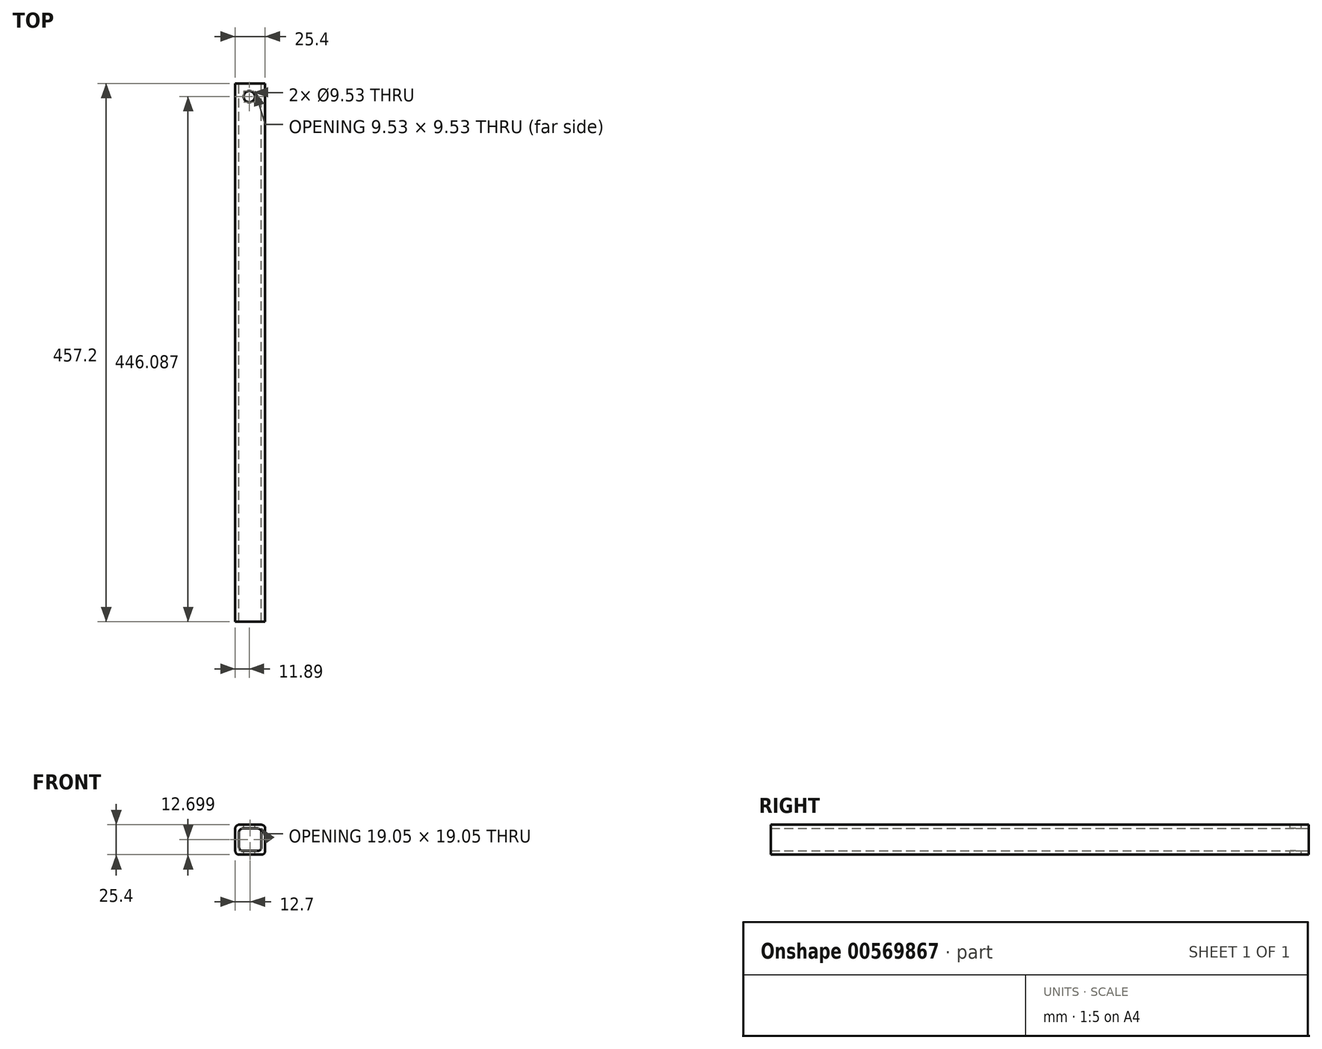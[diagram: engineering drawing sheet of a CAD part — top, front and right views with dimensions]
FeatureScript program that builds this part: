
annotation { "Feature Type Name" : "Feature", "Feature Type Description" : "" }
export const myFeature = defineFeature(function(context is Context, id is Id, definition is map)
    precondition{}
    {
        {
            var Q0;
            Q0=qCreatedBy(makeId("Front.planeOp"),FACE);
            var sketch = newSketch(context, id + "F0", { "sketchPlane" : qUnion([Q0])});
            skLineSegment(sketch, "E0.bottom", {"start": v(10.33, -12.26) * mm, "end": v(-8.72, -12.26) * mm});
            skLineSegment(sketch, "E0.top", {"start": v(10.33, 13.14) * mm, "end": v(-8.72, 13.14) * mm});
            skLineSegment(sketch, "E0.left", {"start": v(13.5, -9.09) * mm, "end": v(13.5, 9.96) * mm});
            skLineSegment(sketch, "E0.right", {"start": v(-11.9, -9.09) * mm, "end": v(-11.9, 9.96) * mm});
            skLineSegment(sketch, "E1.bottom", {"start": v(7.16, -9.09) * mm, "end": v(-5.54, -9.09) * mm});
            skLineSegment(sketch, "E1.top", {"start": v(7.16, 9.96) * mm, "end": v(-5.54, 9.96) * mm});
            skLineSegment(sketch, "E1.left", {"start": v(10.33, -5.91) * mm, "end": v(10.33, 6.79) * mm});
            skLineSegment(sketch, "E1.right", {"start": v(-8.72, -5.91) * mm, "end": v(-8.72, 6.79) * mm});
            skPoint(sketch, "E2.visualSharp", {"position": v(10.33, 9.96) * mm});
            skArc(sketch, "E2.filletArc", {"start": v(10.33, 6.79) * mm, "mid": v(9.4, 9.03) * mm, "end": v(7.16, 9.96) * mm});
            skPoint(sketch, "E3.visualSharp", {"position": v(-8.72, 9.96) * mm});
            skArc(sketch, "E3.filletArc", {"start": v(-5.54, 9.96) * mm, "mid": v(-7.79, 9.03) * mm, "end": v(-8.72, 6.79) * mm});
            skPoint(sketch, "E4.visualSharp", {"position": v(-8.72, -9.09) * mm});
            skArc(sketch, "E4.filletArc", {"start": v(-8.72, -5.91) * mm, "mid": v(-7.79, -8.16) * mm, "end": v(-5.54, -9.09) * mm});
            skPoint(sketch, "E5.visualSharp", {"position": v(10.33, -9.09) * mm});
            skArc(sketch, "E5.filletArc", {"start": v(7.16, -9.09) * mm, "mid": v(9.4, -8.16) * mm, "end": v(10.33, -5.91) * mm});
            skPoint(sketch, "E6.visualSharp", {"position": v(13.5, 13.14) * mm});
            skArc(sketch, "E6.filletArc", {"start": v(13.5, 9.96) * mm, "mid": v(12.58, 12.2) * mm, "end": v(10.33, 13.14) * mm});
            skPoint(sketch, "E7.visualSharp", {"position": v(-11.9, 13.14) * mm});
            skArc(sketch, "E7.filletArc", {"start": v(-8.72, 13.14) * mm, "mid": v(-10.96, 12.2) * mm, "end": v(-11.9, 9.96) * mm});
            skPoint(sketch, "E8.visualSharp", {"position": v(-11.9, -12.26) * mm});
            skArc(sketch, "E8.filletArc", {"start": v(-11.9, -9.09) * mm, "mid": v(-10.96, -11.33) * mm, "end": v(-8.72, -12.26) * mm});
            skPoint(sketch, "E9.visualSharp", {"position": v(13.5, -12.26) * mm});
            skArc(sketch, "E9.filletArc", {"start": v(10.33, -12.26) * mm, "mid": v(12.58, -11.33) * mm, "end": v(13.5, -9.09) * mm});
            skSolve(sketch);
        }
        {
            var Q0;
            Q0 = qSketchRegion(id + "F0", true);
            extrude(context, id + "F1", {"entities" : qUnion([Q0]), "depth" : 457.2 * mm, "offsetDistance" : 25.4 * mm});
        }
        {
            var Q0;
            Q0=makeQuery(id+"F1.opExtrude","SWEPT_FACE",FACE,{"disambiguationData":[OSD([sQuery(id+"F0.wireOp",EDGE,"E0.top")])]});
            var sketch = newSketch(context, id + "F2", { "sketchPlane" : qUnion([Q0])});
            skCircle(sketch, "E10", {"center": v(0, -11.11) * mm, "radius": 4.76 * mm});
            skSolve(sketch);
        }
        {
            var Q0;
            Q0=makeQuery(id+"F2.imprint","IMPRINT",FACE,{"disambiguationData":[TD([[makeQuery(id+"F2.imprint","IMPRINT",EDGE,{"derivedFrom":sQuery(id+"F2.wireOp",EDGE,"E10")}),1.0]])]});
            extrude(context, id + "F3", {"entities" : qUnion([Q0]), "operationType" : NewBodyOperationType.REMOVE, "oppositeDirection" : true, "depth" : 25.4 * mm, "offsetDistance" : 25.4 * mm});
        }
    });
